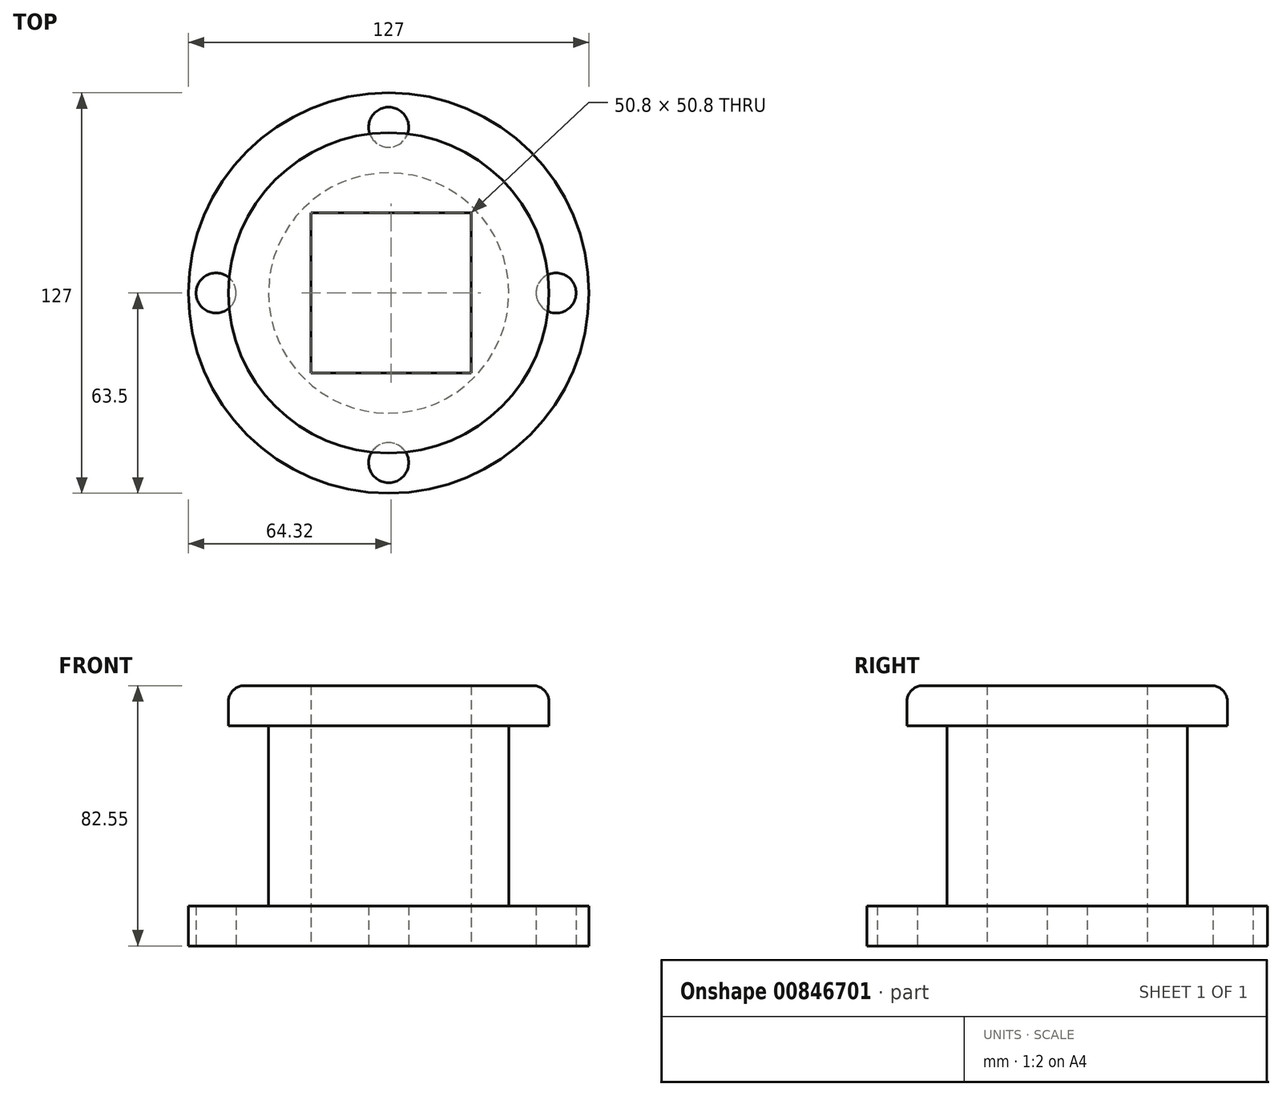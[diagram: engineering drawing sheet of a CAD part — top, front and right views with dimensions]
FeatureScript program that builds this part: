
annotation { "Feature Type Name" : "Feature", "Feature Type Description" : "" }
export const myFeature = defineFeature(function(context is Context, id is Id, definition is map)
    precondition{}
    {
        {
            var Q0;
            Q0=qCreatedBy(makeId("Top.planeOp"),FACE);
            var sketch = newSketch(context, id + "F0", { "sketchPlane" : qUnion([Q0])});
            skLineSegment(sketch, "E0.bottom", {"start": v(-24.58, 25.4) * mm, "end": v(26.22, 25.4) * mm});
            skLineSegment(sketch, "E0.top", {"start": v(-24.58, -25.4) * mm, "end": v(26.22, -25.4) * mm});
            skLineSegment(sketch, "E0.left", {"start": v(-24.58, 25.4) * mm, "end": v(-24.58, -25.4) * mm});
            skLineSegment(sketch, "E0.right", {"start": v(26.22, 25.4) * mm, "end": v(26.22, -25.4) * mm});
            skCircle(sketch, "E1", {"center": v(0, 0) * mm, "radius": 50.8 * mm});
            skSolve(sketch);
        }
        {
            var Q0;
            Q0=makeQuery(id+"F0.imprint","IMPRINT",FACE,{"disambiguationData":[TD([[makeQuery(id+"F0.imprint","IMPRINT",EDGE,{"derivedFrom":sQuery(id+"F0.wireOp",EDGE,"E0.bottom")}),1.0]])]});
            extrude(context, id + "F1", {"entities" : qUnion([Q0]), "depth" : 12.7 * mm, "offsetDistance" : 25.4 * mm});
        }
        {
            var Q0;
            Q0=makeQuery(id+"F1.opExtrude","CAP_EDGE",EDGE,{"disambiguationData":[OSD([sQuery(id+"F0.wireOp",EDGE,"E1")])],"isStart":false});
            fillet(context, id + "F2", {"entities" : qUnion([Q0]), "radius" : 5.08 * mm, "tangentPropagation" : true, "allowEdgeOverflow" : false});
        }
        {
            var Q0;
            Q0=makeQuery(id+"F1.opExtrude","CAP_FACE",FACE,{"disambiguationData":[OSD([sQuery(id+"F0.wireOp",EDGE,"E0.bottom"),sQuery(id+"F0.wireOp",EDGE,"E0.top"),sQuery(id+"F0.wireOp",EDGE,"E0.left"),sQuery(id+"F0.wireOp",EDGE,"E0.right"),sQuery(id+"F0.wireOp",EDGE,"E1")])],"isStart":true});
            var sketch = newSketch(context, id + "F3", { "sketchPlane" : qUnion([Q0])});
            skCircle(sketch, "E2", {"center": v(0, 0) * mm, "radius": 38.1 * mm});
            skSolve(sketch);
        }
        {
            var Q0;
            Q0 = qSketchRegion(id + "F3", true);
            extrude(context, id + "F4", {"entities" : qUnion([Q0]), "operationType" : NewBodyOperationType.ADD, "depth" : 57.15 * mm, "offsetDistance" : 25.4 * mm});
        }
        {
            var Q0;
            Q0=makeQuery(id+"F4.opExtrude","CAP_FACE",FACE,{"disambiguationData":[OSD([sQuery(id+"F3.wireOp",EDGE,"E2")])],"isStart":false});
            var sketch = newSketch(context, id + "F5", { "sketchPlane" : qUnion([Q0])});
            skCircle(sketch, "E3", {"center": v(0, 0) * mm, "radius": 63.5 * mm});
            skSolve(sketch);
        }
        {
            var Q0;
            Q0 = qSketchRegion(id + "F5", true);
            var Q1;
            Q1=makeQuery(id+"F4.opExtrude","CAP_FACE",FACE,{"disambiguationData":[OSD([sQuery(id+"F3.wireOp",EDGE,"E2")])],"isStart":true});
            extrude(context, id + "F6", {"entities" : qUnion([Q0, Q1]), "operationType" : NewBodyOperationType.ADD, "depth" : 12.7 * mm, "offsetDistance" : 25.4 * mm});
        }
        {
            var Q0;
            Q0=makeQuery(id+"F4.opExtrude","CAP_FACE",FACE,{"disambiguationData":[OSD([sQuery(id+"F3.wireOp",EDGE,"E2")])],"isStart":true});
            extrude(context, id + "F7", {"entities" : qUnion([Q0]), "operationType" : NewBodyOperationType.REMOVE, "oppositeDirection" : true, "depth" : 106.68 * mm, "offsetDistance" : 25.4 * mm});
        }
        {
            var Q0;
            Q0=makeQuery(id+"F6.opExtrude","CAP_FACE",FACE,{"disambiguationData":[OSD([sQuery(id+"F5.wireOp",EDGE,"E3")])],"isStart":false});
            var sketch = newSketch(context, id + "F8", { "sketchPlane" : qUnion([Q0])});
            skCircle(sketch, "E4", {"center": v(-54.72, 0) * mm, "radius": 6.35 * mm});
            skCircle(sketch, "E5", {"center": v(0, 53.81) * mm, "radius": 6.35 * mm});
            skCircle(sketch, "E6", {"center": v(53.1, 0) * mm, "radius": 6.35 * mm});
            skCircle(sketch, "E7", {"center": v(0, -52.6) * mm, "radius": 6.35 * mm});
            skSolve(sketch);
        }
        {
            var Q0;
            Q0=makeQuery(id+"F8.imprint","IMPRINT",FACE,{"disambiguationData":[TD([[makeQuery(id+"F8.imprint","IMPRINT",EDGE,{"derivedFrom":sQuery(id+"F8.wireOp",EDGE,"E7")}),1.0]])]});
            var Q1;
            Q1=makeQuery(id+"F8.imprint","IMPRINT",FACE,{"disambiguationData":[TD([[makeQuery(id+"F8.imprint","IMPRINT",EDGE,{"derivedFrom":sQuery(id+"F8.wireOp",EDGE,"E6")}),1.0]])]});
            var Q2;
            Q2=makeQuery(id+"F8.imprint","IMPRINT",FACE,{"disambiguationData":[TD([[makeQuery(id+"F8.imprint","IMPRINT",EDGE,{"derivedFrom":sQuery(id+"F8.wireOp",EDGE,"E5")}),1.0]])]});
            var Q3;
            Q3=makeQuery(id+"F8.imprint","IMPRINT",FACE,{"disambiguationData":[TD([[makeQuery(id+"F8.imprint","IMPRINT",EDGE,{"derivedFrom":sQuery(id+"F8.wireOp",EDGE,"E4")}),1.0]])]});
            extrude(context, id + "F9", {"entities" : qUnion([Q0, Q1, Q2, Q3]), "operationType" : NewBodyOperationType.REMOVE, "oppositeDirection" : true, "depth" : 12.7 * mm, "offsetDistance" : 25.4 * mm});
        }
    });
